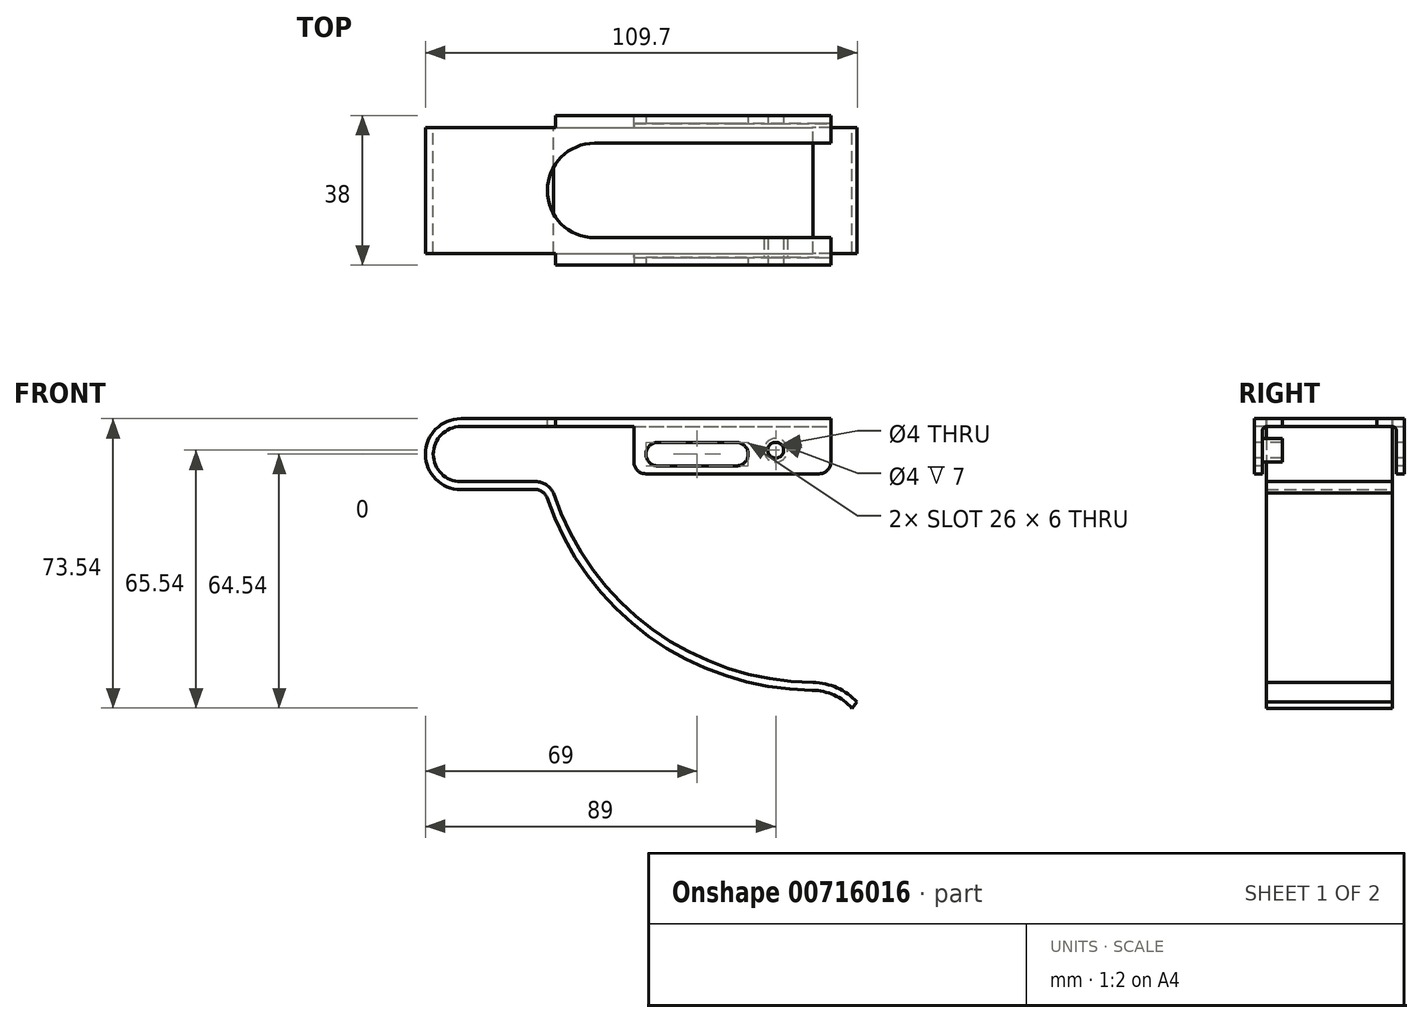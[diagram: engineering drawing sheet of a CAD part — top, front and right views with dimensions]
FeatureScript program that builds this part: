
annotation { "Feature Type Name" : "Feature", "Feature Type Description" : "" }
export const myFeature = defineFeature(function(context is Context, id is Id, definition is map)
    precondition{}
    {
        {
            var Q0;
            Q0=qCreatedBy(makeId("Front.planeOp"),FACE);
            var sketch = newSketch(context, id + "F0", { "sketchPlane" : qUnion([Q0])});
            skArc(sketch, "E0", {"start": v(0, 9) * mm, "mid": v(-9, 0) * mm, "end": v(0, -9) * mm});
            skLineSegment(sketch, "E1", {"start": v(0, 9) * mm, "end": v(94, 9) * mm});
            skLineSegment(sketch, "E2", {"start": v(0, -9) * mm, "end": v(19, -9) * mm});
            skArc(sketch, "E3", {"start": v(21.84, -11.04) * mm, "mid": v(47.74, -46.27) * mm, "end": v(89.26, -60) * mm});
            skArc(sketch, "E4", {"start": v(99.4, -64.54) * mm, "mid": v(94.8, -61.22) * mm, "end": v(89.26, -60) * mm});
            skPoint(sketch, "E5.visualSharp", {"position": v(21.19, -9) * mm});
            skArc(sketch, "E5.filletArc", {"start": v(21.84, -11.04) * mm, "mid": v(20.75, -9.56) * mm, "end": v(19, -9) * mm});
            skLineSegment(sketch, "E6.0", {"start": v(0, 7) * mm, "end": v(94, 7) * mm});
            skArc(sketch, "E6.1", {"start": v(0, 7) * mm, "mid": v(-7, 0) * mm, "end": v(0, -7) * mm});
            skArc(sketch, "E6.2", {"start": v(100.7, -63) * mm, "mid": v(95.59, -59.38) * mm, "end": v(89.47, -58) * mm});
            skArc(sketch, "E6.3", {"start": v(23.52, -9.85) * mm, "mid": v(48.75, -44.54) * mm, "end": v(89.47, -58) * mm});
            skArc(sketch, "E6.4", {"start": v(23.52, -9.85) * mm, "mid": v(21.67, -7.77) * mm, "end": v(19, -7) * mm});
            skLineSegment(sketch, "E6.5", {"start": v(0, -7) * mm, "end": v(19, -7) * mm});
            skLineSegment(sketch, "E7", {"start": v(94, 9) * mm, "end": v(94, 7) * mm});
            skLineSegment(sketch, "E8", {"start": v(99.4, -64.54) * mm, "end": v(100.7, -63) * mm});
            skLineSegment(sketch, "E9", {"start": v(100.7, -63) * mm, "end": v(129.57, -63) * mm});
            skSolve(sketch);
        }
        {
            var Q0;
            Q0 = qSketchRegion(id + "F0", true);
            extrude(context, id + "F1", {"entities" : qUnion([Q0]), "depth" : 16 * mm, "offsetDistance" : 25 * mm});
        }
        {
            var Q0;
            Q0=makeQuery(id+"F1.opExtrude","SWEPT_FACE",FACE,{"disambiguationData":[OSD([sQuery(id+"F0.wireOp",EDGE,"E1")])]});
            var sketch = newSketch(context, id + "F2", { "sketchPlane" : qUnion([Q0])});
            skLineSegment(sketch, "E10.bottom", {"start": v(24, -16) * mm, "end": v(94, -16) * mm});
            skLineSegment(sketch, "E10.top", {"start": v(24, -19) * mm, "end": v(94, -19) * mm});
            skLineSegment(sketch, "E10.left", {"start": v(24, -16) * mm, "end": v(24, -19) * mm});
            skLineSegment(sketch, "E10.right", {"start": v(94, -16) * mm, "end": v(94, -19) * mm});
            skSolve(sketch);
        }
        {
            var Q0;
            Q0 = qSketchRegion(id + "F2", true);
            extrude(context, id + "F3", {"entities" : qUnion([Q0]), "operationType" : NewBodyOperationType.ADD, "oppositeDirection" : true, "depth" : 2 * mm, "offsetDistance" : 25 * mm});
        }
        {
            var Q0;
            Q0=makeQuery(id+"F3.opExtrude","SWEPT_FACE",FACE,{"disambiguationData":[OSD([sQuery(id+"F2.wireOp",EDGE,"E10.top")])]});
            var sketch = newSketch(context, id + "F4", { "sketchPlane" : qUnion([Q0])});
            skLineSegment(sketch, "E11.bottom", {"start": v(94, 9) * mm, "end": v(44, 9) * mm});
            skLineSegment(sketch, "E11.top", {"start": v(94, -5) * mm, "end": v(44, -5) * mm});
            skLineSegment(sketch, "E11.left", {"start": v(94, 9) * mm, "end": v(94, -5) * mm});
            skLineSegment(sketch, "E11.right", {"start": v(44, 9) * mm, "end": v(44, -5) * mm});
            skSolve(sketch);
        }
        {
            var Q0;
            Q0 = qSketchRegion(id + "F4", true);
            extrude(context, id + "F5", {"entities" : qUnion([Q0]), "operationType" : NewBodyOperationType.ADD, "oppositeDirection" : true, "depth" : 2 * mm, "offsetDistance" : 25 * mm});
        }
        {
            var Q0;
            Q0=makeQuery(id+"F5.boolean.opBoolean","INTERSECT",EDGE,{"derivedFrom":[makeQuery(id+"F3.boolean.opBoolean","MERGE",FACE,{"derivedFrom":[makeQuery(id+"F1.opExtrude","SWEPT_FACE",FACE,{"disambiguationData":[OSD([sQuery(id+"F0.wireOp",EDGE,"E6.0")])]}),makeQuery(id+"F3.opExtrude","CAP_FACE",FACE,{"disambiguationData":[OSD([sQuery(id+"F2.wireOp",EDGE,"E10.bottom"),sQuery(id+"F2.wireOp",EDGE,"E10.top"),sQuery(id+"F2.wireOp",EDGE,"E10.left"),sQuery(id+"F2.wireOp",EDGE,"E10.right")])],"isStart":false})]}),makeQuery(id+"F5.opExtrude","CAP_FACE",FACE,{"disambiguationData":[OSD([sQuery(id+"F4.wireOp",EDGE,"E11.bottom"),sQuery(id+"F4.wireOp",EDGE,"E11.top"),sQuery(id+"F4.wireOp",EDGE,"E11.left"),sQuery(id+"F4.wireOp",EDGE,"E11.right")])],"isStart":false})]});
            fillet(context, id + "F6", {"entities" : qUnion([Q0]), "radius" : 1 * mm, "allowEdgeOverflow" : false});
        }
        {
            var Q0;
            Q0=makeQuery(id+"F1.opExtrude","SWEPT_BODY",BODY,{"disambiguationData":[OSD([sQuery(id+"F0.wireOp",EDGE,"E0"),sQuery(id+"F0.wireOp",EDGE,"E1"),sQuery(id+"F0.wireOp",EDGE,"E2"),sQuery(id+"F0.wireOp",EDGE,"E3"),sQuery(id+"F0.wireOp",EDGE,"E4"),sQuery(id+"F0.wireOp",EDGE,"E5.filletArc"),sQuery(id+"F0.wireOp",EDGE,"E6.0"),sQuery(id+"F0.wireOp",EDGE,"E6.1"),sQuery(id+"F0.wireOp",EDGE,"E6.2"),sQuery(id+"F0.wireOp",EDGE,"E6.3"),sQuery(id+"F0.wireOp",EDGE,"E6.4"),sQuery(id+"F0.wireOp",EDGE,"E6.5"),sQuery(id+"F0.wireOp",EDGE,"E7"),sQuery(id+"F0.wireOp",EDGE,"E8")])]});
            var Q1;
            Q1=qCreatedBy(makeId("Front.planeOp"),FACE);
            mirror(context, id + "F7", {"operationType" : NewBodyOperationType.ADD, "entities" : qUnion([Q0]), "mirrorPlane" : qUnion([Q1])});
        }
        {
            var Q0;
            {var subQ0=makeQuery(id+"F3.boolean.opBoolean","MERGE",FACE,{"derivedFrom":[makeQuery(id+"F1.opExtrude","SWEPT_FACE",FACE,{"disambiguationData":[OSD([sQuery(id+"F0.wireOp",EDGE,"E1")])]}),makeQuery(id+"F3.opExtrude","CAP_FACE",FACE,{"disambiguationData":[OSD([sQuery(id+"F2.wireOp",EDGE,"E10.bottom"),sQuery(id+"F2.wireOp",EDGE,"E10.top"),sQuery(id+"F2.wireOp",EDGE,"E10.left"),sQuery(id+"F2.wireOp",EDGE,"E10.right")])],"isStart":true})]});Q0=makeQuery(id+"F7.boolean.opBoolean","MERGE",FACE,{"derivedFrom":[subQ0,makeQuery(id+"F7.opPattern","COPY",FACE,{"derivedFrom":subQ0,"instanceName":"1"})]});}
            var sketch = newSketch(context, id + "F8", { "sketchPlane" : qUnion([Q0])});
            skArc(sketch, "E12", {"start": v(34, 12) * mm, "mid": v(22, 0) * mm, "end": v(34, -12) * mm});
            skLineSegment(sketch, "E13", {"start": v(34, 12) * mm, "end": v(94, 12) * mm});
            skLineSegment(sketch, "E14", {"start": v(34, -12) * mm, "end": v(94, -12) * mm});
            skSolve(sketch);
        }
        {
            var Q0;
            Q0 = qSketchRegion(id + "F8", true);
            var Q1;
            Q1=makeQuery(id+"F8.imprint","IMPRINT",FACE,{"disambiguationData":[TD([[makeQuery(id+"F8.imprint","IMPRINT",EDGE,{"derivedFrom":sQuery(id+"F8.wireOp",EDGE,"E12")}),1.0]])]});
            extrude(context, id + "F9", {"entities" : qUnion([Q0, Q1]), "operationType" : NewBodyOperationType.REMOVE, "oppositeDirection" : true, "depth" : 2 * mm, "offsetDistance" : 25 * mm});
        }
        {
            var Q0;
            Q0=makeQuery(id+"F5.boolean.opBoolean","MERGE",FACE,{"derivedFrom":[makeQuery(id+"F3.opExtrude","SWEPT_FACE",FACE,{"disambiguationData":[OSD([sQuery(id+"F2.wireOp",EDGE,"E10.top")])]}),makeQuery(id+"F5.opExtrude","CAP_FACE",FACE,{"disambiguationData":[OSD([sQuery(id+"F4.wireOp",EDGE,"E11.bottom"),sQuery(id+"F4.wireOp",EDGE,"E11.top"),sQuery(id+"F4.wireOp",EDGE,"E11.left"),sQuery(id+"F4.wireOp",EDGE,"E11.right")])],"isStart":true})]});
            var sketch = newSketch(context, id + "F10", { "sketchPlane" : qUnion([Q0])});
            skLineSegment(sketch, "E15", {"start": v(50, 0) * mm, "end": v(70, 0) * mm});
            skArc(sketch, "E16.0.startCap", {"start": v(50, -3) * mm, "mid": v(47, 0) * mm, "end": v(50, 3) * mm});
            skArc(sketch, "E16.0.endCap", {"start": v(70, 3) * mm, "mid": v(73, 0) * mm, "end": v(70, -3) * mm});
            skLineSegment(sketch, "E16.0.left", {"start": v(50, 3) * mm, "end": v(70, 3) * mm});
            skLineSegment(sketch, "E16.0.right", {"start": v(50, -3) * mm, "end": v(70, -3) * mm});
            skSolve(sketch);
        }
        {
            var Q0;
            Q0 = qSketchRegion(id + "F10", true);
            extrude(context, id + "F11", {"entities" : qUnion([Q0]), "operationType" : NewBodyOperationType.REMOVE, "endBound" : BoundingType.THROUGH_ALL, "oppositeDirection" : true, "depth" : 25 * mm, "offsetDistance" : 25 * mm});
        }
        {
            var Q0;
            Q0=makeQuery(id+"F5.boolean.opBoolean","MERGE",FACE,{"derivedFrom":[makeQuery(id+"F3.opExtrude","SWEPT_FACE",FACE,{"disambiguationData":[OSD([sQuery(id+"F2.wireOp",EDGE,"E10.top")])]}),makeQuery(id+"F5.opExtrude","CAP_FACE",FACE,{"disambiguationData":[OSD([sQuery(id+"F4.wireOp",EDGE,"E11.bottom"),sQuery(id+"F4.wireOp",EDGE,"E11.top"),sQuery(id+"F4.wireOp",EDGE,"E11.left"),sQuery(id+"F4.wireOp",EDGE,"E11.right")])],"isStart":true})]});
            var sketch = newSketch(context, id + "F12", { "sketchPlane" : qUnion([Q0])});
            skPoint(sketch, "E17", {"position": v(80, 1) * mm});
            skSolve(sketch);
        }
        {
            var Q0;
            Q0=sQuery(id+"F12.wireOp",VERTEX,"E17");
            var Q1;
            Q1=makeQuery(id+"F1.opExtrude","SWEPT_BODY",BODY,{"disambiguationData":[OSD([sQuery(id+"F0.wireOp",EDGE,"E0"),sQuery(id+"F0.wireOp",EDGE,"E1"),sQuery(id+"F0.wireOp",EDGE,"E2"),sQuery(id+"F0.wireOp",EDGE,"E3"),sQuery(id+"F0.wireOp",EDGE,"E4"),sQuery(id+"F0.wireOp",EDGE,"E5.filletArc"),sQuery(id+"F0.wireOp",EDGE,"E6.0"),sQuery(id+"F0.wireOp",EDGE,"E6.1"),sQuery(id+"F0.wireOp",EDGE,"E6.2"),sQuery(id+"F0.wireOp",EDGE,"E6.3"),sQuery(id+"F0.wireOp",EDGE,"E6.4"),sQuery(id+"F0.wireOp",EDGE,"E6.5"),sQuery(id+"F0.wireOp",EDGE,"E7"),sQuery(id+"F0.wireOp",EDGE,"E8")])]});
            hole(context, id + "F13", {"style" : HoleStyle.SIMPLE, "endStyle" : HoleEndStyle.THROUGH, "holeDiameter" : 4 * mm, "majorDiameter" : 5 * mm, "isTappedThrough" : true, "tappedDepth" : 12 * mm, "tapClearance" : 3, "locations" : qUnion([Q0]), "scope" : qUnion([Q1])});
        }
        {
            var Q0;
            Q0=makeQuery(id+"F5.opExtrude","CAP_FACE",FACE,{"disambiguationData":[OSD([sQuery(id+"F4.wireOp",EDGE,"E11.bottom"),sQuery(id+"F4.wireOp",EDGE,"E11.top"),sQuery(id+"F4.wireOp",EDGE,"E11.left"),sQuery(id+"F4.wireOp",EDGE,"E11.right")])],"isStart":false});
            var sketch = newSketch(context, id + "F14", { "sketchPlane" : qUnion([Q0])});
            skCircle(sketch, "E18.0", {"center": v(-80, 1) * mm, "radius": 2 * mm});
            skCircle(sketch, "E19.0", {"center": v(-80, 1) * mm, "radius": 3 * mm});
            skSolve(sketch);
        }
        {
            var Q0;
            Q0 = qSketchRegion(id + "F14", true);
            extrude(context, id + "F15", {"entities" : qUnion([Q0]), "operationType" : NewBodyOperationType.ADD, "depth" : 5 * mm, "offsetDistance" : 25 * mm});
        }
        {
            var Q0;
            Q0=makeQuery(id+"F5.opExtrude","SWEPT_EDGE",EDGE,{"disambiguationData":[OSD([sQuery(id+"F4.wireOp",EDGE,"E11.top"),sQuery(id+"F4.wireOp",EDGE,"E11.left")])]});
            var Q1;
            Q1=makeQuery(id+"F5.opExtrude","SWEPT_EDGE",EDGE,{"disambiguationData":[OSD([sQuery(id+"F4.wireOp",EDGE,"E11.top"),sQuery(id+"F4.wireOp",EDGE,"E11.right")])]});
            var Q2;
            Q2=makeQuery(id+"F7.opPattern","COPY",EDGE,{"derivedFrom":makeQuery(id+"F5.opExtrude","SWEPT_EDGE",EDGE,{"disambiguationData":[OSD([sQuery(id+"F4.wireOp",EDGE,"E11.top"),sQuery(id+"F4.wireOp",EDGE,"E11.left")])]}),"instanceName":"1"});
            var Q3;
            Q3=makeQuery(id+"F7.opPattern","COPY",EDGE,{"derivedFrom":makeQuery(id+"F5.opExtrude","SWEPT_EDGE",EDGE,{"disambiguationData":[OSD([sQuery(id+"F4.wireOp",EDGE,"E11.top"),sQuery(id+"F4.wireOp",EDGE,"E11.right")])]}),"instanceName":"1"});
            fillet(context, id + "F16", {"entities" : qUnion([Q0, Q1, Q2, Q3]), "radius" : 3 * mm, "tangentPropagation" : true, "allowEdgeOverflow" : false});
        }
    });
